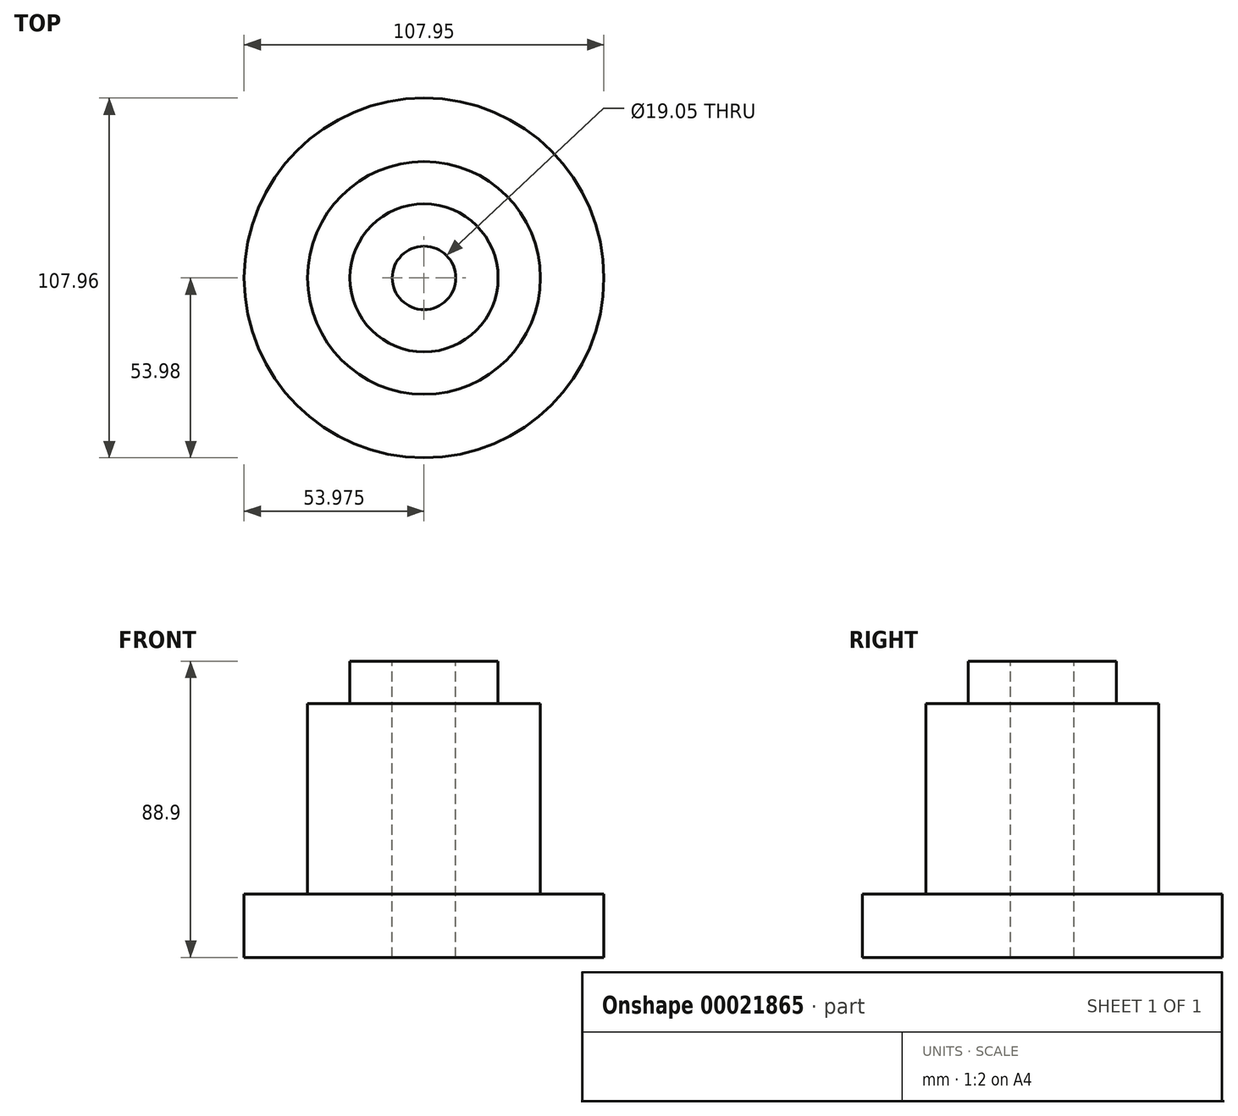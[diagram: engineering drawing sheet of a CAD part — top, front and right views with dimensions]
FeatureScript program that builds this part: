
annotation { "Feature Type Name" : "Feature", "Feature Type Description" : "" }
export const myFeature = defineFeature(function(context is Context, id is Id, definition is map)
    precondition{}
    {
        {
            var Q0;
            Q0=qCreatedBy(makeId("Front.planeOp"),FACE);
            var sketch = newSketch(context, id + "F0", { "sketchPlane" : qUnion([Q0])});
            skLineSegment(sketch, "E0", {"start": v(0, 49.78) * mm, "end": v(44.45, 49.78) * mm});
            skLineSegment(sketch, "E1", {"start": v(0, 49.78) * mm, "end": v(0, 138.68) * mm});
            skLineSegment(sketch, "E2", {"start": v(44.45, 49.78) * mm, "end": v(44.45, 68.83) * mm});
            skLineSegment(sketch, "E3", {"start": v(44.45, 68.83) * mm, "end": v(25.4, 68.83) * mm});
            skLineSegment(sketch, "E4", {"start": v(25.4, 68.83) * mm, "end": v(25.4, 125.98) * mm});
            skLineSegment(sketch, "E5", {"start": v(25.4, 125.98) * mm, "end": v(12.7, 125.98) * mm});
            skLineSegment(sketch, "E6", {"start": v(12.7, 125.98) * mm, "end": v(12.7, 138.68) * mm});
            skLineSegment(sketch, "E7", {"start": v(12.7, 138.68) * mm, "end": v(0, 138.68) * mm});
            skLineSegment(sketch, "E8", {"start": v(-9.52, 138.68) * mm, "end": v(-9.52, 49.78) * mm});
            skSolve(sketch);
        }
        {
            var Q0;
            Q0=makeQuery(id+"F0.imprint","IMPRINT",FACE,{"disambiguationData":[TD([[makeQuery(id+"F0.imprint","IMPRINT",EDGE,{"derivedFrom":sQuery(id+"F0.wireOp",EDGE,"E0")}),1.0]])]});
            var Q1;
            Q1=sQuery(id+"F0.wireOp",EDGE,"E8");
            revolve(context, id + "F1", {"entities" : qUnion([Q0]), "axis" : qUnion([Q1]), "revolveType" : RevolveType.FULL});
        }
    });
